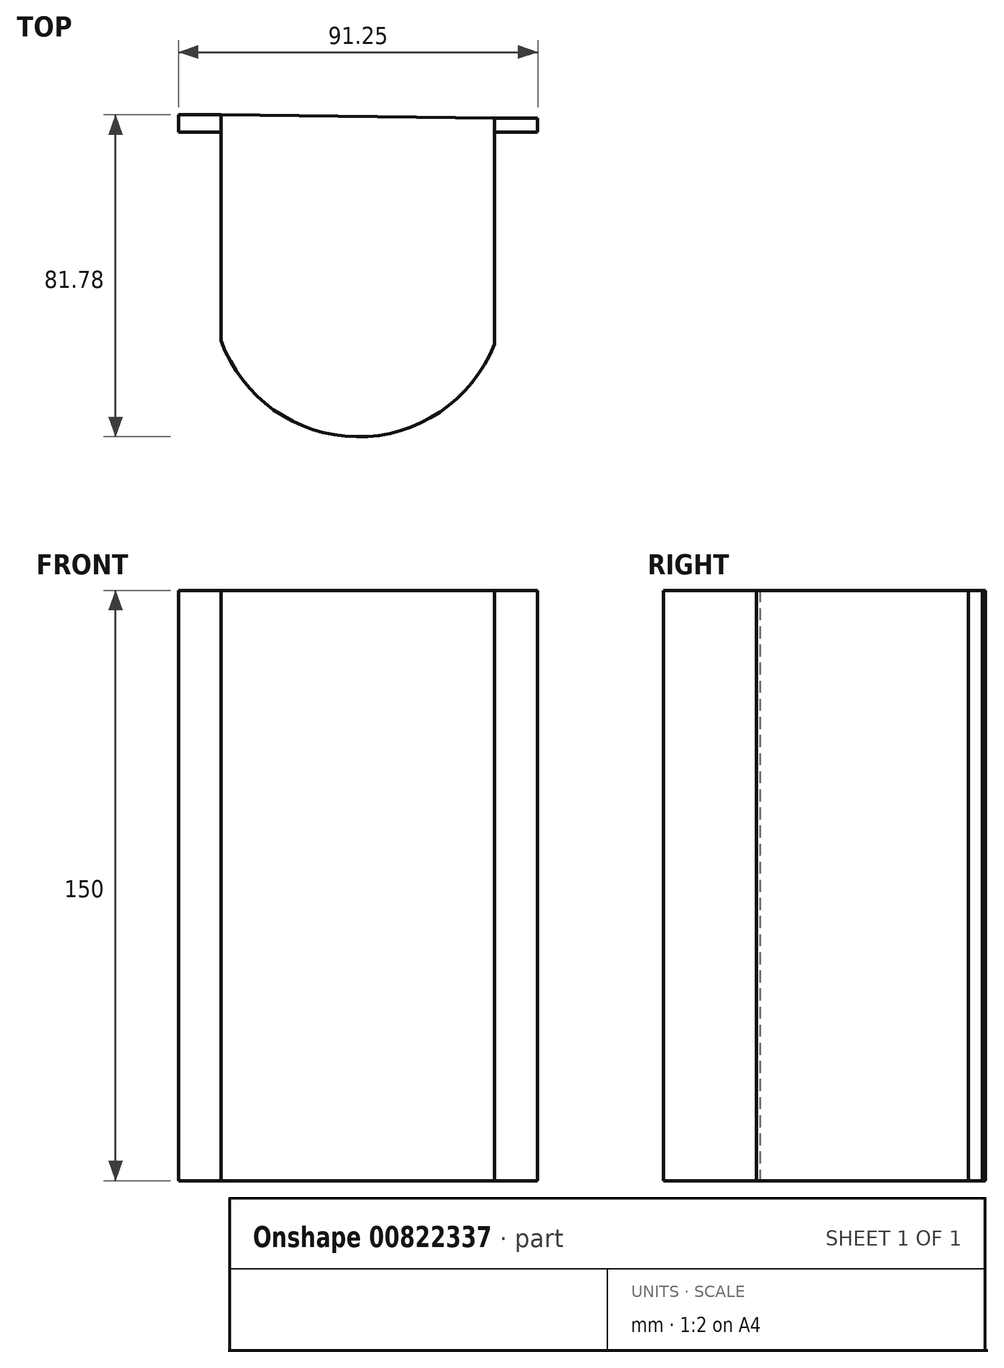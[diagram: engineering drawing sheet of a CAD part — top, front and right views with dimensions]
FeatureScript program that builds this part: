
annotation { "Feature Type Name" : "Feature", "Feature Type Description" : "" }
export const myFeature = defineFeature(function(context is Context, id is Id, definition is map)
    precondition{}
    {
        {
            var Q0;
            Q0=qCreatedBy(makeId("Top.planeOp"),FACE);
            var sketch = newSketch(context, id + "F0", { "sketchPlane" : qUnion([Q0])});
            skLineSegment(sketch, "E0.bottom", {"start": v(34.72, 28.25) * mm, "end": v(-34.73, 29.12) * mm});
            skLineSegment(sketch, "E0.left", {"start": v(34.72, 28.25) * mm, "end": v(34.73, -29.12) * mm});
            skLineSegment(sketch, "E0.right", {"start": v(-34.73, 29.12) * mm, "end": v(-34.72, -28.25) * mm});
            skPoint(sketch, "E0.middle", {"position": v(0, 0) * mm});
            skArc(sketch, "E1", {"start": v(-34.72, -28.25) * mm, "mid": v(-0.3, -52.66) * mm, "end": v(34.73, -29.12) * mm});
            skLineSegment(sketch, "E2.bottom", {"start": v(-34.73, 29.12) * mm, "end": v(-45.5, 29.12) * mm});
            skLineSegment(sketch, "E2.top", {"start": v(-34.73, 24.75) * mm, "end": v(-45.5, 24.75) * mm});
            skLineSegment(sketch, "E2.left", {"start": v(-34.73, 29.12) * mm, "end": v(-34.73, 24.75) * mm});
            skLineSegment(sketch, "E2.right", {"start": v(-45.5, 29.12) * mm, "end": v(-45.5, 24.75) * mm});
            skLineSegment(sketch, "E3.bottom", {"start": v(34.72, 28.25) * mm, "end": v(45.75, 28.25) * mm});
            skLineSegment(sketch, "E3.top", {"start": v(34.72, 24.75) * mm, "end": v(45.75, 24.75) * mm});
            skLineSegment(sketch, "E3.left", {"start": v(34.72, 28.25) * mm, "end": v(34.72, 24.75) * mm});
            skLineSegment(sketch, "E3.right", {"start": v(45.75, 28.25) * mm, "end": v(45.75, 24.75) * mm});
            skSolve(sketch);
        }
        {
            var Q0;
            Q0=makeQuery(id+"F0.imprint","IMPRINT",FACE,{"disambiguationData":[TD([[makeQuery(id+"F0.imprint","IMPRINT",EDGE,{"derivedFrom":sQuery(id+"F0.wireOp",EDGE,"E2.bottom")}),1.0]])]});
            var Q1;
            Q1=makeQuery(id+"F0.imprint","IMPRINT",FACE,{"disambiguationData":[TD([[makeQuery(id+"F0.imprint","IMPRINT",EDGE,{"derivedFrom":sQuery(id+"F0.wireOp",EDGE,"E0.bottom")}),1.0]])]});
            var Q2;
            {var subQ0=sQuery(id+"F0.wireOp",EDGE,"E3.bottom");Q2=makeQuery(id+"F0.imprint","IMPRINT",FACE,{"disambiguationData":[TD([[makeQuery(id+"F0.imprint","IMPRINT",EDGE,{"derivedFrom":subQ0}),-1.0]])]});}
            extrude(context, id + "F1", {"entities" : qUnion([Q0, Q1, Q2]), "depth" : 150 * mm, "offsetDistance" : 25 * mm});
        }
    });
